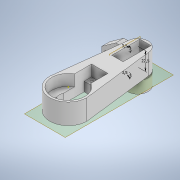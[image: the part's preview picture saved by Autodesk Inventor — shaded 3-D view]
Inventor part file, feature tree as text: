
AUTODESK INVENTOR PART (.ipt)
format: ipt  version: 2021 (Build 250183000, 183)  size: 413,184 bytes
history: native  units: mm
features: sketch x33, extrude x28, plane x2
ambient origin geometry x8: Origin, YZ Plane, XZ Plane, XY Plane, X Axis, Y Axis, Z Axis, Center Point
bodies: Solid1 (feature_tree)
feature tree (63):
  sketch  "Sketch1"  dims[d0=46.398mm d1=25.5mm d2=0.0mm]
  extrude  "Extrusion1"  Depth=25.5mm TaperAngle=0.0deg
  extrude  "Extrusion2"  Depth=25.5mm TaperAngle=0.0deg
  extrude  "Extrusion3"  Depth=14.0mm TaperAngle=0.0deg
  extrude  "Extrusion4"  Depth=30.0mm TaperAngle=0.0deg
  extrude  "Extrusion5"  Depth=10.25mm
  extrude  "Extrusion6"  Depth=49.736mm
  extrude  "Extrusion7"  Depth=30.0mm TaperAngle=0.0deg
  extrude  "Extrusion8"  Depth=14.0mm TaperAngle=0.0deg
  sketch  "Sketch11"  dims[d24=3.5mm d25=4.556mm]
  sketch  "Sketch12"  dims[d26=3.5mm d27=5.072mm]
  extrude  "Extrusion9"  Depth=4.556mm
  sketch  "Sketch13"  dims[d28=4.556mm d29=4.556mm]
  extrude  "Extrusion10"  Depth=4.556mm
  extrude  "Extrusion11"  Depth=5.072mm
  extrude  "Extrusion12"  Depth=4.556mm
  extrude  "Extrusion13"  Depth=3.5mm
  extrude  "Extrusion14"  Depth=25.5mm
  extrude  "Extrusion15"  Depth=25.5mm
  extrude  "Extrusion16"  Depth=25.5mm
  extrude  "Extrusion17"  Depth=40.0mm
  extrude  "Extrusion18"  Depth=35.0mm
  sketch  "Sketch29"  dims[d54=3.5mm d55=40.0mm d56=0.0mm]
  sketch  "Sketch30"  dims[d57=5.0mm d58=5.0mm]
  plane  "Work Plane1"
  extrude  "Extrusion19"  Depth=2.5mm
  plane  "Work Plane2"
  extrude  "Extrusion20"  Depth=2.5mm
  extrude  "Extrusion21"  Depth=40.0mm TaperAngle=0.0deg
  extrude  "Extrusion22"  Depth=5.0mm
  extrude  "Extrusion23"  Depth=5.5mm TaperAngle=0.0deg
  extrude  "Extrusion24"  Depth=25.5mm
  extrude  "Extrusion25"  Depth=7.0mm
  extrude  "Extrusion26"  Depth=29.75mm TaperAngle=0.0deg
  sketch  "Sketch40"  dims[d83=3.5mm]
  extrude  "Extrusion27"  Depth=5.5mm
  extrude  "Extrusion28"  Depth=2.5mm
  sketch  "Sketch45"  dims[d86=1.75mm d87=15.0mm d88=0.0mm d89=-1.5mm d90=9.25mm d91=4.25mm d92=0.0mm d93=0.0mm d94=10.0mm d95=25.0mm d96=0.0mm d97=12.5mm d98=12.5mm d99=10.0mm d100=0.0mm d103=10.0mm d104=0.0mm d105=5.0mm d106=6.25mm d107=6.25mm d108=3.3mm d109=3.3mm d110=13.75mm d111=0.0mm d112=10.0mm d113=10.0mm d114=10.0mm d115=0.0mm d116=22.5mm d117=10.0mm d118=10.0mm d119=10.0mm d120=0.0mm d121=3.5mm d122=3.5mm d123=10.0mm d124=0.0mm d125=10.0mm d126=0.0mm d134=22.5mm d136=5.0mm d137=5.0mm d138=3.5mm d139=3.5mm d46=0.872665mm d140=0.5mm d141=0.872665mm d142=0.5mm d143=0.872665mm]
  sketch  "Sketch2"  dims[d3=110.0mm d4=25.5mm d5=0.0mm]
  sketch  "Sketch3"  dims[d6=41.33mm d7=14.0mm d8=0.0mm]
  sketch  "Sketch4"  dims[d9=22.23mm d10=30.0mm d11=0.0mm]
  sketch  "Sketch5"  dims[d12=10.5mm d13=10.25mm]
  sketch  "Sketch6"  dims[d14=20.5mm d15=49.736mm]
  sketch  "Sketch7"  dims[d16=40.5mm d17=30.0mm d18=0.0mm]
  sketch  "Sketch9"  dims[d19=9.236mm d20=14.0mm d21=0.0mm]
  sketch  "Sketch10"  dims[d22=5.072mm d23=4.556mm]
  sketch  "Sketch15"  dims[d30=3.5mm d31=3.5mm]
  sketch  "Sketch17"  dims[d32=1450.0mm d33=0.0mm d34=25.5mm]
  sketch  "Sketch18"  dims[d35=25.5mm d36=0.0mm d37=25.5mm]
  sketch  "Sketch20"  dims[d38=25.5mm d39=0.0mm d40=20.0mm]
  sketch  "Sketch23"  dims[d41=20.0mm d42=0.0mm d43=40.0mm]
  sketch  "Sketch24"  dims[d44=40.0mm d45=0.0mm d48=35.0mm]
  sketch  "Sketch25"  dims[d49=5.0mm d51=2.5mm]
  sketch  "Sketch27"  dims[d52=3.5mm d53=2.5mm]
  sketch  "Sketch31"  dims[d59=10.0mm d60=0.0mm d61=5.5mm d62=0.0mm]
  sketch  "Sketch32"  dims[d63=25.5mm d64=0.0mm d65=4.0mm]
  sketch  "Sketch33"  dims[d66=20.0mm d70=7.0mm]
  sketch  "Sketch34"  dims[d71=7.0mm d72=29.75mm d73=0.0mm]
  sketch  "Sketch36"  dims[d76=5.5mm d77=5.5mm]
  sketch  "Sketch37"  dims[d78=15.5mm d79=0.0mm d80=2.5mm]
  sketch  "Sketch38"  dims[d81=3.5mm]
  sketch  "Sketch39"  dims[d82=2.5mm]
  sketch  "Sketch41"  dims[d84=10.0mm d85=0.0mm]
